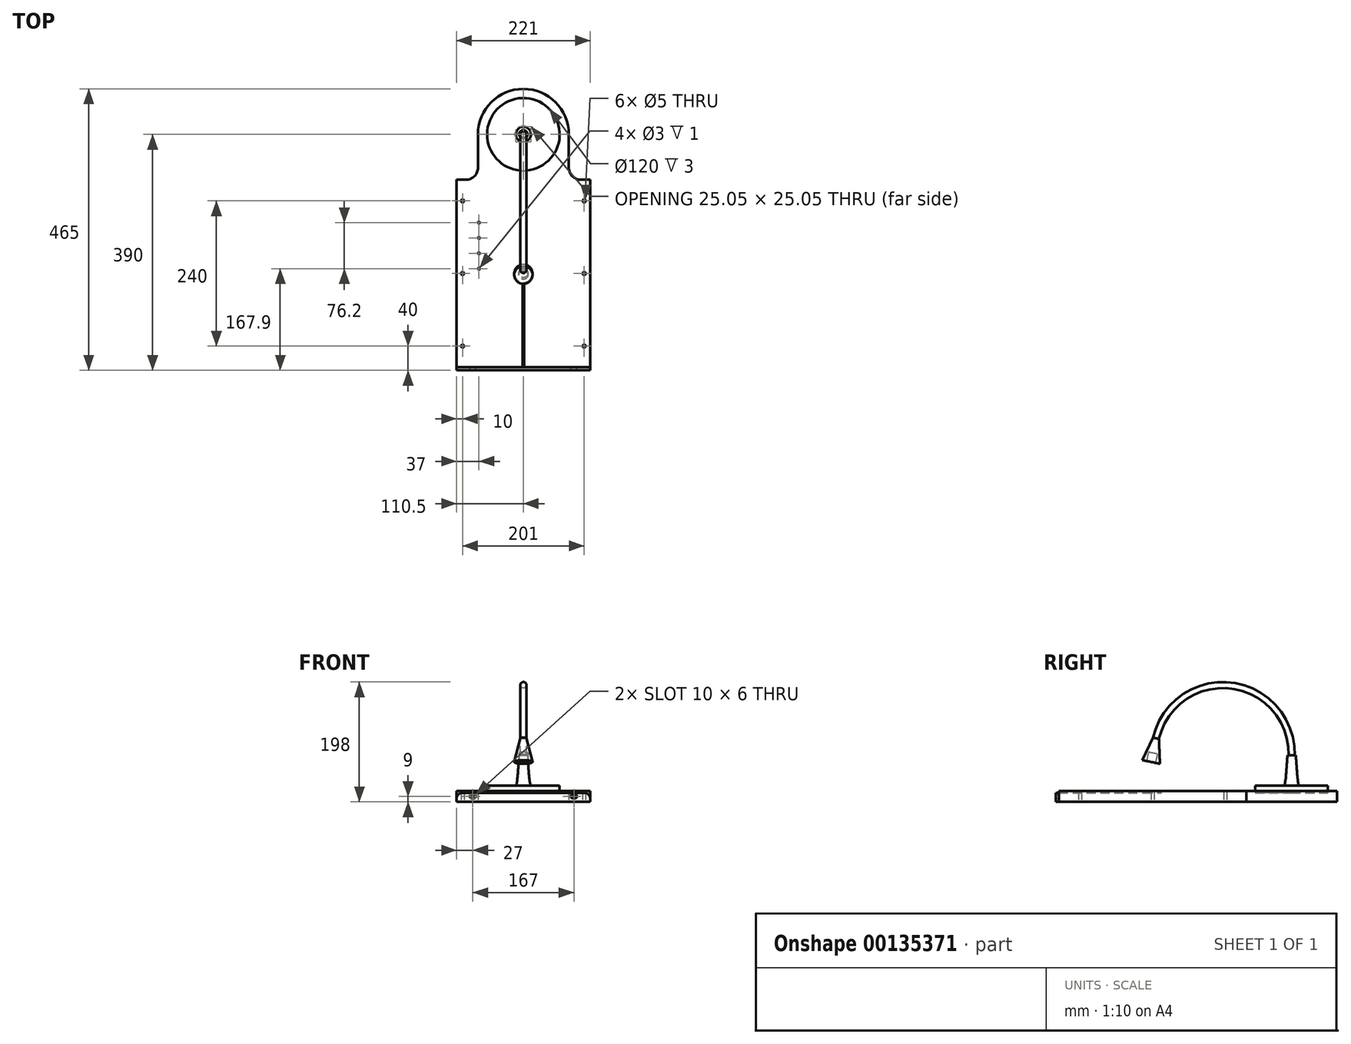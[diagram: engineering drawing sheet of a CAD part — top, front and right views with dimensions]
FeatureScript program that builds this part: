
annotation { "Feature Type Name" : "Feature", "Feature Type Description" : "" }
export const myFeature = defineFeature(function(context is Context, id is Id, definition is map)
    precondition{}
    {
        {
            var Q0;
            Q0=qCreatedBy(makeId("Top.planeOp"),FACE);
            var sketch = newSketch(context, id + "F0", { "sketchPlane" : qUnion([Q0])});
            skCircle(sketch, "E0", {"center": v(10, 35) * mm, "radius": 2.5 * mm});
            skCircle(sketch, "E1.0.1.0", {"center": v(10, 155) * mm, "radius": 2.5 * mm});
            skCircle(sketch, "E1.0.2.0", {"center": v(10, 275) * mm, "radius": 2.5 * mm});
            skCircle(sketch, "E1.1.0.0", {"center": v(211, 35) * mm, "radius": 2.5 * mm});
            skCircle(sketch, "E1.1.1.0", {"center": v(211, 155) * mm, "radius": 2.5 * mm});
            skCircle(sketch, "E1.1.2.0", {"center": v(211, 275) * mm, "radius": 2.5 * mm});
            skLineSegment(sketch, "E1.direction1", {"start": v(10, 35) * mm, "end": v(211, 35) * mm, "construction": true});
            skLineSegment(sketch, "E1.direction2", {"start": v(10, 35) * mm, "end": v(10, 155) * mm, "construction": true});
            skLineSegment(sketch, "E2.bottom", {"start": v(0, 0) * mm, "end": v(221, 0) * mm});
            skLineSegment(sketch, "E2.left", {"start": v(0, 0) * mm, "end": v(0, 310) * mm});
            skLineSegment(sketch, "E2.right", {"start": v(221, 0) * mm, "end": v(221, 310) * mm});
            skCircle(sketch, "E3", {"center": v(110.5, 385) * mm, "radius": 60 * mm, "construction": true});
            skPoint(sketch, "E3.centerSnap0", {"position": v(110.5, 460) * mm});
            skPoint(sketch, "E4.visualSharp", {"position": v(35.5, 310) * mm});
            skPoint(sketch, "E5.visualSharp", {"position": v(185.5, 310) * mm});
            skPoint(sketch, "E6.orphan", {"position": v(0, 460) * mm});
            skPoint(sketch, "E7.orphan", {"position": v(221, 460) * mm});
            skArc(sketch, "E8", {"start": v(185.5, 385) * mm, "mid": v(110.5, 460) * mm, "end": v(35.5, 385) * mm});
            skLineSegment(sketch, "E9", {"start": v(35.5, 385) * mm, "end": v(35.5, 330) * mm});
            skLineSegment(sketch, "E10", {"start": v(0, 310) * mm, "end": v(15.5, 310) * mm});
            skLineSegment(sketch, "E11", {"start": v(185.5, 385) * mm, "end": v(185.5, 330) * mm});
            skLineSegment(sketch, "E12", {"start": v(205.5, 310) * mm, "end": v(221, 310) * mm});
            skArc(sketch, "E13.filletArc", {"start": v(15.5, 310) * mm, "mid": v(29.64, 315.86) * mm, "end": v(35.5, 330) * mm});
            skArc(sketch, "E14.filletArc", {"start": v(185.5, 330) * mm, "mid": v(191.36, 315.86) * mm, "end": v(205.5, 310) * mm});
            skSolve(sketch);
        }
        {
            var Q0;
            Q0 = qSketchRegion(id + "F0", true);
            extrude(context, id + "F1", {"entities" : qUnion([Q0]), "depth" : 18 * mm});
        }
        {
            var Q0;
            Q0=makeQuery(id+"F1.opExtrude","CAP_FACE",FACE,{"disambiguationData":[OSD([sQuery(id+"F0.wireOp",EDGE,"WMVPhm4Y-LSUh-PGYy-xByu-pg97ZHc04cBP.left"),sQuery(id+"F0.wireOp",EDGE,"WMVPhm4Y-LSUh-PGYy-xByu-pg97ZHc04cBP.right"),sQuery(id+"F0.wireOp",EDGE,"E0"),sQuery(id+"F0.wireOp",EDGE,"E1.0.1.0"),sQuery(id+"F0.wireOp",EDGE,"E1.0.2.0"),sQuery(id+"F0.wireOp",EDGE,"E1.1.0.0"),sQuery(id+"F0.wireOp",EDGE,"E1.1.1.0"),sQuery(id+"F0.wireOp",EDGE,"E1.1.2.0"),sQuery(id+"F0.wireOp",EDGE,"Chv08MVR-3Lne-9AID-vyQp-ACr5yz1igclO.top"),sQuery(id+"F0.wireOp",EDGE,"Chv08MVR-3Lne-9AID-vyQp-ACr5yz1igclO.left"),sQuery(id+"F0.wireOp",EDGE,"Chv08MVR-3Lne-9AID-vyQp-ACr5yz1igclO.right"),sQuery(id+"F0.wireOp",EDGE,"dq3pKR3A-HWKQ-b0KG-mNNH-Xo0HHrndQ5vF")])],"isStart":false});
            var sketch = newSketch(context, id + "F2", { "sketchPlane" : qUnion([Q0])});
            skArc(sketch, "E15", {"start": v(112, 140.08) * mm, "mid": v(110.5, 170) * mm, "end": v(109, 140.08) * mm});
            skLineSegment(sketch, "E16", {"start": v(109, 0) * mm, "end": v(109, 140.08) * mm});
            skLineSegment(sketch, "E17", {"start": v(112, 140.08) * mm, "end": v(112, 0) * mm});
            skLineSegment(sketch, "E18", {"start": v(109, 0) * mm, "end": v(112, 0) * mm});
            skCircle(sketch, "E19", {"center": v(37, 162.9) * mm, "radius": 1.5 * mm});
            skCircle(sketch, "E20.0.1.0", {"center": v(37, 188.3) * mm, "radius": 1.5 * mm});
            skCircle(sketch, "E20.0.2.0", {"center": v(37, 213.7) * mm, "radius": 1.5 * mm});
            skCircle(sketch, "E20.0.3.0", {"center": v(37, 239.1) * mm, "radius": 1.5 * mm});
            skLineSegment(sketch, "E20.direction1", {"start": v(37, 162.9) * mm, "end": v(110.5, 162.9) * mm, "construction": true});
            skLineSegment(sketch, "E20.direction2", {"start": v(37, 162.9) * mm, "end": v(37, 188.3) * mm, "construction": true});
            skLineSegment(sketch, "E21", {"start": v(110.5, 162.9) * mm, "end": v(110.5, 155) * mm, "construction": true});
            skCircle(sketch, "E22", {"center": v(110.5, 385) * mm, "radius": 60 * mm});
            skSolve(sketch);
        }
        {
            var Q0;
            Q0=makeQuery(id+"F2.imprint","IMPRINT",FACE,{"disambiguationData":[TD([[makeQuery(id+"F2.imprint","IMPRINT",EDGE,{"derivedFrom":sQuery(id+"F2.wireOp",EDGE,"E19")}),1.0]])]});
            var Q1;
            Q1=makeQuery(id+"F2.imprint","IMPRINT",FACE,{"disambiguationData":[TD([[makeQuery(id+"F2.imprint","IMPRINT",EDGE,{"derivedFrom":sQuery(id+"F2.wireOp",EDGE,"E20.0.1.0")}),1.0]])]});
            var Q2;
            Q2=makeQuery(id+"F2.imprint","IMPRINT",FACE,{"disambiguationData":[TD([[makeQuery(id+"F2.imprint","IMPRINT",EDGE,{"derivedFrom":sQuery(id+"F2.wireOp",EDGE,"E20.0.2.0")}),1.0]])]});
            var Q3;
            Q3=makeQuery(id+"F2.imprint","IMPRINT",FACE,{"disambiguationData":[TD([[makeQuery(id+"F2.imprint","IMPRINT",EDGE,{"derivedFrom":sQuery(id+"F2.wireOp",EDGE,"E20.0.3.0")}),1.0]])]});
            extrude(context, id + "F3", {"entities" : qUnion([Q0, Q1, Q2, Q3]), "operationType" : NewBodyOperationType.REMOVE, "oppositeDirection" : true, "depth" : 1 * mm});
        }
        {
            var Q0;
            Q0=makeQuery(id+"F2.imprint","IMPRINT",FACE,{"disambiguationData":[TD([[makeQuery(id+"F2.imprint","IMPRINT",EDGE,{"derivedFrom":sQuery(id+"F2.wireOp",EDGE,"E15")}),1.0]])]});
            var Q1;
            Q1=makeQuery(id+"F2.imprint","IMPRINT",FACE,{"disambiguationData":[TD([[makeQuery(id+"F2.imprint","IMPRINT",EDGE,{"derivedFrom":sQuery(id+"F2.wireOp",EDGE,"518ae5dd-98f1-46e5-8992-a8ad112d0c94")}),1.0]])]});
            var Q2;
            Q2=makeQuery(id+"F2.imprint","IMPRINT",FACE,{"disambiguationData":[TD([[makeQuery(id+"F2.imprint","IMPRINT",EDGE,{"derivedFrom":sQuery(id+"F2.wireOp",EDGE,"E22")}),1.0]])]});
            extrude(context, id + "F4", {"entities" : qUnion([Q0, Q1, Q2]), "operationType" : NewBodyOperationType.REMOVE, "oppositeDirection" : true, "depth" : 3 * mm});
        }
        {
            var Q0;
            Q0=qCreatedBy(makeId("Front.planeOp"),FACE);
            var sketch = newSketch(context, id + "F5", { "sketchPlane" : qUnion([Q0])});
            skLineSegment(sketch, "E23.top", {"start": v(10, 15) * mm, "end": v(211, 15) * mm});
            skLineSegment(sketch, "E23.left", {"start": v(0, 0) * mm, "end": v(0, 5) * mm});
            skLineSegment(sketch, "E23.right", {"start": v(221, 0) * mm, "end": v(221, 5) * mm});
            skArc(sketch, "E24", {"start": v(25, 12) * mm, "mid": v(22, 9) * mm, "end": v(25, 6) * mm});
            skArc(sketch, "E25", {"start": v(29, 6) * mm, "mid": v(32, 9) * mm, "end": v(29, 12) * mm});
            skLineSegment(sketch, "E26", {"start": v(25, 9) * mm, "end": v(29, 9) * mm, "construction": true});
            skLineSegment(sketch, "E27", {"start": v(0, 0) * mm, "end": v(221, 0) * mm});
            skLineSegment(sketch, "E28", {"start": v(25, 12) * mm, "end": v(29, 12) * mm});
            skLineSegment(sketch, "E29", {"start": v(25, 6) * mm, "end": v(29, 6) * mm});
            skPoint(sketch, "E30.visualSharp", {"position": v(0, 15) * mm});
            skArc(sketch, "E30.filletArc", {"start": v(10, 15) * mm, "mid": v(2.93, 12.07) * mm, "end": v(0, 5) * mm});
            skPoint(sketch, "E31.visualSharp", {"position": v(221, 15) * mm});
            skArc(sketch, "E31.filletArc", {"start": v(221, 5) * mm, "mid": v(218.07, 12.07) * mm, "end": v(211, 15) * mm});
            skLineSegment(sketch, "E32", {"start": v(110.5, 15) * mm, "end": v(110.5, 0) * mm, "construction": true});
            skArc(sketch, "E33.MirrorCS", {"start": v(196, 12) * mm, "mid": v(199, 9) * mm, "end": v(196, 6) * mm});
            skLineSegment(sketch, "E34.MirrorCS", {"start": v(196, 6) * mm, "end": v(192, 6) * mm});
            skLineSegment(sketch, "E35.MirrorCS", {"start": v(196, 12) * mm, "end": v(192, 12) * mm});
            skArc(sketch, "E36.MirrorCS", {"start": v(192, 6) * mm, "mid": v(189, 9) * mm, "end": v(192, 12) * mm});
            skSolve(sketch);
        }
        {
            var Q0;
            Q0 = qSketchRegion(id + "F5", true);
            extrude(context, id + "F6", {"entities" : qUnion([Q0]), "depth" : 5 * mm});
        }
        {
            var Q0;
            Q0=qCreatedBy(makeId("Front.planeOp"),FACE);
            cPlane(context, id + "F7", {"entities" : qUnion([Q0]), "cplaneType" : CPlaneType.OFFSET, "offset" : (300 + 10 + 75) * mm, "oppositeDirection" : true, "width" : 150 * mm, "height" : 150 * mm});
        }
        {
            var Q0;
            Q0=qCreatedBy(id+"F7.planeOp",FACE);
            var sketch = newSketch(context, id + "F8", { "sketchPlane" : qUnion([Q0])});
            skLineSegment(sketch, "E37", {"start": v(110.5, 0) * mm, "end": v(110.5, 77) * mm, "construction": true});
            skLineSegment(sketch, "E38", {"start": v(110.5, 15) * mm, "end": v(170.5, 15) * mm});
            skLineSegment(sketch, "E39", {"start": v(170.5, 15) * mm, "end": v(170.5, 27) * mm});
            skLineSegment(sketch, "E40", {"start": v(170.5, 27) * mm, "end": v(123, 27) * mm});
            skLineSegment(sketch, "E41", {"start": v(110.5, 77) * mm, "end": v(117.5, 77) * mm});
            skFitSpline(sketch, "E42", {"points": [v(117.5, 77) * mm, v(123, 27) * mm, v(131.86, 77) * mm], "startDerivative": vector(9.37, -150.12) * mm, "endDerivative": vector(19.34, 149.88) * mm});
            skLineSegment(sketch, "E43", {"start": v(110.5, 77) * mm, "end": v(110.5, 15) * mm});
            skSolve(sketch);
        }
        {
            var Q0;
            Q0=makeQuery(id+"F8.imprint","IMPRINT",FACE,{"disambiguationData":[TD([[makeQuery(id+"F8.imprint","IMPRINT",EDGE,{"derivedFrom":sQuery(id+"F8.wireOp",EDGE,"E38")}),1.0]])]});
            var Q1;
            Q1=sQuery(id+"F8.wireOp",EDGE,"E37");
            revolve(context, id + "F9", {"entities" : qUnion([Q0]), "axis" : qUnion([Q1]), "revolveType" : RevolveType.FULL});
        }
        {
            var Q0;
            Q0=makeQuery(id+"F9.opRevolve","SWEPT_FACE",FACE,{"disambiguationData":[OSD([sQuery(id+"F8.wireOp",EDGE,"E41")])]});
            var sketch = newSketch(context, id + "F10", { "sketchPlane" : qUnion([Q0])});
            skCircle(sketch, "E44", {"center": v(110.5, 385) * mm, "radius": 5 * mm});
            skSolve(sketch);
        }
        {
            var Q0;
            Q0=qCreatedBy(makeId("Right.planeOp"),FACE);
            cPlane(context, id + "F11", {"entities" : qUnion([Q0]), "cplaneType" : CPlaneType.OFFSET, "offset" : 110.5 * mm, "width" : 150 * mm, "height" : 150 * mm});
        }
        {
            var Q0;
            Q0=qCreatedBy(id+"F11.planeOp",FACE);
            var sketch = newSketch(context, id + "F12", { "sketchPlane" : qUnion([Q0])});
            skArc(sketch, "E45", {"start": v(385, 77) * mm, "mid": v(285.51, 192.12) * mm, "end": v(160.77, 105) * mm});
            skSolve(sketch);
        }
        {
            var Q0;
            Q0=makeQuery(id+"F10.imprint","IMPRINT",FACE,{"disambiguationData":[TD([[makeQuery(id+"F10.imprint","IMPRINT",EDGE,{"derivedFrom":sQuery(id+"F10.wireOp",EDGE,"E44")}),1.0]])]});
            var Q1;
            Q1=sQuery(id+"F12.wireOp",EDGE,"E45");
            sweep(context, id + "F13", {"operationType" : NewBodyOperationType.ADD, "profiles" : qUnion([Q0]), "path" : qUnion([Q1])});
        }
        {
            var Q0;
            Q0=makeQuery(id+"F13.opSweep","CAP_FACE",FACE,{"disambiguationData":[OSD([sQuery(id+"F10.wireOp",EDGE,"E44"),sQuery(id+"F12.wireOp",VERTEX,"E45.end")])],"isStart":false});
            cPlane(context, id + "F14", {"entities" : qUnion([Q0]), "cplaneType" : CPlaneType.OFFSET, "offset" : 40 * mm, "width" : 150 * mm, "height" : 150 * mm});
        }
        {
            var Q0;
            Q0=qCreatedBy(id+"F14.planeOp",FACE);
            var sketch = newSketch(context, id + "F15", { "sketchPlane" : qUnion([Q0])});
            skCircle(sketch, "E46", {"center": v(110.5, -135.9) * mm, "radius": 15 * mm});
            skSolve(sketch);
        }
        {
            var Q1;
            Q1=makeQuery(id+"F15.imprint","IMPRINT",FACE,{"disambiguationData":[TD([[makeQuery(id+"F15.imprint","IMPRINT",EDGE,{"derivedFrom":sQuery(id+"F15.wireOp",EDGE,"E46")}),1.0]])]});
            var Q2;
            Q2=makeQuery(id+"F13.opSweep","CAP_FACE",FACE,{"disambiguationData":[OSD([sQuery(id+"F10.wireOp",EDGE,"E44"),sQuery(id+"F12.wireOp",VERTEX,"E45.end")])],"isStart":false});
            loft(context, id + "F16", {"operationType" : NewBodyOperationType.ADD, "sheetProfilesArray" : [{ "sheetProfileEntities" : qUnion([Q1]) }, { "sheetProfileEntities" : qUnion([Q2]) }]});
        }
        {
            var Q0;
            Q0=makeQuery(id+"F16.opLoft","CAP_FACE",FACE,{"disambiguationData":[OSD([makeQuery(id+"F15.imprint","IMPRINT",FACE,{"disambiguationData":[TD([[makeQuery(id+"F15.imprint","IMPRINT",EDGE,{"derivedFrom":sQuery(id+"F15.wireOp",EDGE,"E46")}),1.0]])]})])],"isStart":true});
            var sketch = newSketch(context, id + "F17", { "sketchPlane" : qUnion([Q0])});
            skCircle(sketch, "E47", {"center": v(110.5, -135.9) * mm, "radius": 7.5 * mm});
            skSolve(sketch);
        }
        {
            var Q0;
            Q0 = qSketchRegion(id + "F17", true);
            extrude(context, id + "F18", {"entities" : qUnion([Q0]), "operationType" : NewBodyOperationType.REMOVE, "oppositeDirection" : true, "depth" : 15 * mm});
        }
    });
